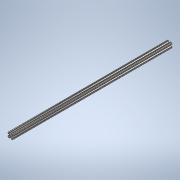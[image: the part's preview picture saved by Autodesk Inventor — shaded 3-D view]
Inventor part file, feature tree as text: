
AUTODESK INVENTOR PART (.ipt)
format: ipt  version: 2020 (Build 240168000, 168)  size: 244,736 bytes
history: native  units: in
note: dims shown in document units (in); Inventor stores cm internally (conversion verified against a paired STEP export)
features: extrude x1, sketch x1
ambient origin geometry x8: Origin, YZ Plane, XZ Plane, XY Plane, X Axis, Y Axis, Z Axis, Center Point
bodies: Solid1 (feature_tree)
feature tree (2):
  extrude  "Extrusion1"  [1 undecoded]
  sketch  "Sketch1"  dims[d0=32.0in d1=0.0in]
note: 1 required parameter value undecoded (feature->parameter linkage not recoverable at this tier; creation-order binding heuristic only, values carry confidence <= 0.55)
